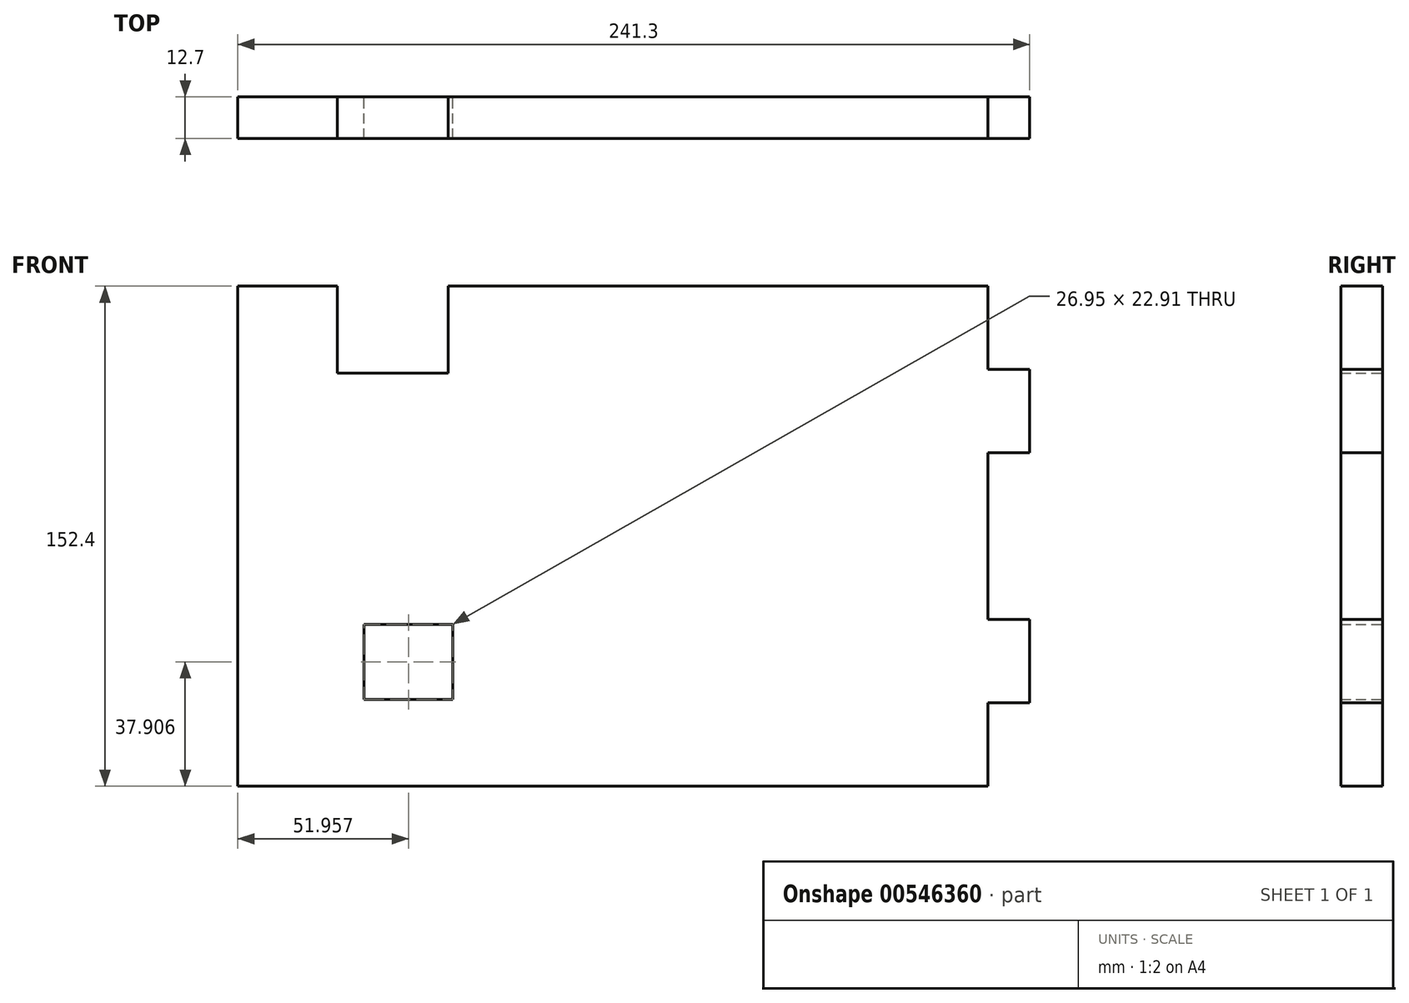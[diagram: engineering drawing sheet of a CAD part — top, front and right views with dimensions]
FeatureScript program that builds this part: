
annotation { "Feature Type Name" : "Feature", "Feature Type Description" : "" }
export const myFeature = defineFeature(function(context is Context, id is Id, definition is map)
    precondition{}
    {
        {
            var Q0;
            Q0=qCreatedBy(makeId("Front.planeOp"),FACE);
            var sketch = newSketch(context, id + "F0", { "sketchPlane" : qUnion([Q0])});
            skLineSegment(sketch, "E0.bottom", {"start": v(107.95, 76.2) * mm, "end": v(-56.63, 76.2) * mm});
            skLineSegment(sketch, "E0.top", {"start": v(107.95, -76.2) * mm, "end": v(-120.65, -76.2) * mm});
            skLineSegment(sketch, "E0.left", {"start": v(120.65, 50.8) * mm, "end": v(120.65, 25.4) * mm});
            skLineSegment(sketch, "E0.right", {"start": v(-120.65, 76.2) * mm, "end": v(-120.65, -76.2) * mm});
            skPoint(sketch, "E0.middle", {"position": v(0, 0) * mm});
            skLineSegment(sketch, "E1", {"start": v(107.95, 76.2) * mm, "end": v(107.95, 50.8) * mm});
            skLineSegment(sketch, "E2", {"start": v(107.95, 50.8) * mm, "end": v(120.65, 50.8) * mm});
            skLineSegment(sketch, "E3", {"start": v(120.65, 25.4) * mm, "end": v(107.95, 25.4) * mm});
            skLineSegment(sketch, "E4", {"start": v(107.95, 25.4) * mm, "end": v(107.95, -25.4) * mm});
            skLineSegment(sketch, "E5", {"start": v(107.95, -25.4) * mm, "end": v(120.65, -25.4) * mm});
            skLineSegment(sketch, "E6", {"start": v(120.65, -25.4) * mm, "end": v(120.65, -50.8) * mm});
            skLineSegment(sketch, "E7", {"start": v(120.65, -50.8) * mm, "end": v(107.95, -50.8) * mm});
            skLineSegment(sketch, "E8", {"start": v(107.95, -50.8) * mm, "end": v(107.95, -76.2) * mm});
            skLineSegment(sketch, "E9", {"start": v(-90.32, 76.2) * mm, "end": v(-90.32, 49.64) * mm});
            skLineSegment(sketch, "E10", {"start": v(-90.32, 49.64) * mm, "end": v(-56.63, 49.64) * mm});
            skLineSegment(sketch, "E11", {"start": v(-56.63, 49.64) * mm, "end": v(-56.63, 76.2) * mm});
            skLineSegment(sketch, "E12", {"start": v(-82.17, -26.84) * mm, "end": v(-55.22, -26.84) * mm});
            skLineSegment(sketch, "E13", {"start": v(-55.22, -26.84) * mm, "end": v(-55.22, -49.75) * mm});
            skLineSegment(sketch, "E14", {"start": v(-55.22, -49.75) * mm, "end": v(-82.17, -49.75) * mm});
            skLineSegment(sketch, "E15", {"start": v(-82.17, -49.75) * mm, "end": v(-82.17, -26.84) * mm});
            skPoint(sketch, "E16.orphan", {"position": v(120.65, 76.2) * mm});
            skPoint(sketch, "E17.orphan", {"position": v(120.65, -76.2) * mm});
            skLineSegment(sketch, "E18.trimOffspring", {"start": v(-90.32, 76.2) * mm, "end": v(-120.65, 76.2) * mm});
            skSolve(sketch);
        }
        {
            var Q0;
            Q0 = qSketchRegion(id + "F0", true);
            extrude(context, id + "F1", {"entities" : qUnion([Q0]), "endBound" : BoundingType.SYMMETRIC, "depth" : 12.7 * mm, "offsetDistance" : 25.4 * mm});
        }
    });
